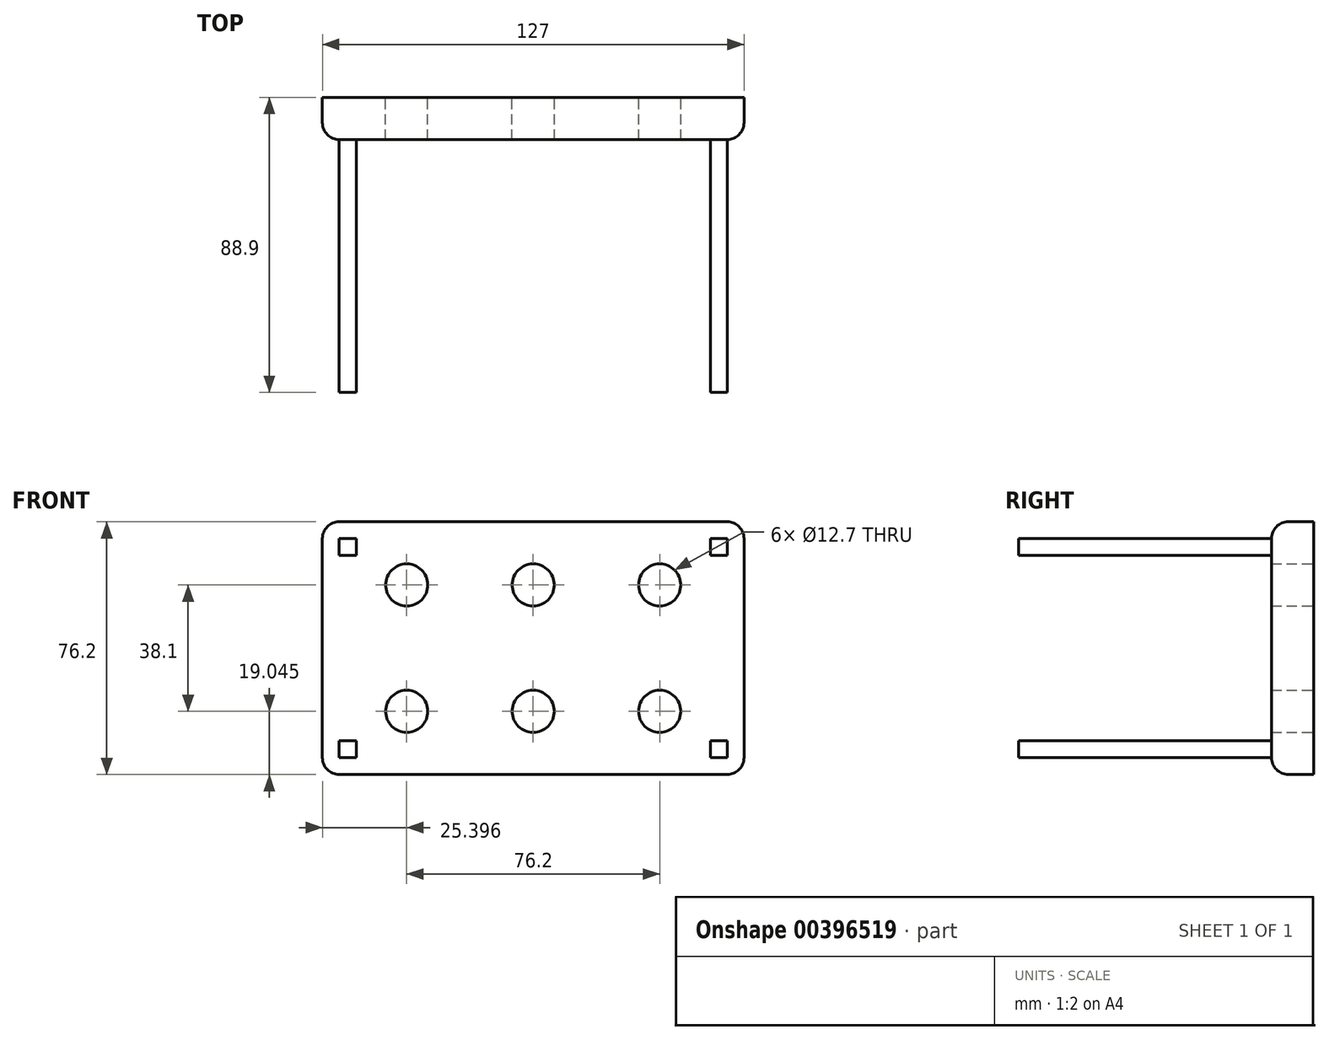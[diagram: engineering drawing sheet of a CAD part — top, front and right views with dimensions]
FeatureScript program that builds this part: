
annotation { "Feature Type Name" : "Feature", "Feature Type Description" : "" }
export const myFeature = defineFeature(function(context is Context, id is Id, definition is map)
    precondition{}
    {
        {
            var Q0;
            Q0=qCreatedBy(makeId("Front.planeOp"),FACE);
            var sketch = newSketch(context, id + "F0", { "sketchPlane" : qUnion([Q0])});
            skLineSegment(sketch, "E0.bottom", {"start": v(-63.95, 33.6) * mm, "end": v(63.05, 33.6) * mm});
            skLineSegment(sketch, "E0.top", {"start": v(-63.95, -42.6) * mm, "end": v(63.05, -42.6) * mm});
            skLineSegment(sketch, "E0.left", {"start": v(-63.95, 33.6) * mm, "end": v(-63.95, -42.6) * mm});
            skLineSegment(sketch, "E0.right", {"start": v(63.05, 33.6) * mm, "end": v(63.05, -42.6) * mm});
            skCircle(sketch, "E1", {"center": v(-38.55, 14.56) * mm, "radius": 6.35 * mm});
            skCircle(sketch, "E2", {"center": v(-0.45, 14.56) * mm, "radius": 6.35 * mm});
            skCircle(sketch, "E3", {"center": v(37.65, 14.56) * mm, "radius": 6.35 * mm});
            skCircle(sketch, "E4", {"center": v(-38.55, -23.54) * mm, "radius": 6.35 * mm});
            skCircle(sketch, "E5", {"center": v(-0.45, -23.54) * mm, "radius": 6.35 * mm});
            skCircle(sketch, "E6", {"center": v(37.65, -23.54) * mm, "radius": 6.35 * mm});
            skSolve(sketch);
        }
        {
            var Q0;
            Q0=makeQuery(id+"F0.imprint","IMPRINT",FACE,{"disambiguationData":[TD([[makeQuery(id+"F0.imprint","IMPRINT",EDGE,{"derivedFrom":sQuery(id+"F0.wireOp",EDGE,"E0.bottom")}),-1.0]])]});
            extrude(context, id + "F1", {"entities" : qUnion([Q0]), "depth" : 12.7 * mm});
        }
        {
            var Q0;
            Q0=makeQuery(id+"F1.opExtrude","CAP_EDGE",EDGE,{"disambiguationData":[OSD([sQuery(id+"F0.wireOp",EDGE,"E0.bottom")])],"isStart":false});
            var Q1;
            Q1=makeQuery(id+"F1.opExtrude","CAP_EDGE",EDGE,{"disambiguationData":[OSD([sQuery(id+"F0.wireOp",EDGE,"E0.left")])],"isStart":false});
            var Q2;
            Q2=makeQuery(id+"F1.opExtrude","CAP_EDGE",EDGE,{"disambiguationData":[OSD([sQuery(id+"F0.wireOp",EDGE,"E0.top")])],"isStart":false});
            var Q3;
            Q3=makeQuery(id+"F1.opExtrude","CAP_EDGE",EDGE,{"disambiguationData":[OSD([sQuery(id+"F0.wireOp",EDGE,"E0.right")])],"isStart":false});
            fillet(context, id + "F2", {"entities" : qUnion([Q0, Q1, Q2, Q3]), "radius" : 5.08 * mm, "tangentPropagation" : true, "allowEdgeOverflow" : false});
        }
        {
            var Q0;
            Q0=makeQuery(id+"F1.opExtrude","SWEPT_EDGE",EDGE,{"disambiguationData":[OSD([sQuery(id+"F0.wireOp",EDGE,"E0.top"),sQuery(id+"F0.wireOp",EDGE,"E0.left")])]});
            var Q1;
            Q1=makeQuery(id+"F1.opExtrude","SWEPT_EDGE",EDGE,{"disambiguationData":[OSD([sQuery(id+"F0.wireOp",EDGE,"E0.top"),sQuery(id+"F0.wireOp",EDGE,"E0.right")])]});
            var Q2;
            Q2=makeQuery(id+"F1.opExtrude","SWEPT_EDGE",EDGE,{"disambiguationData":[OSD([sQuery(id+"F0.wireOp",EDGE,"E0.bottom"),sQuery(id+"F0.wireOp",EDGE,"E0.right")])]});
            var Q3;
            Q3=makeQuery(id+"F1.opExtrude","SWEPT_EDGE",EDGE,{"disambiguationData":[OSD([sQuery(id+"F0.wireOp",EDGE,"E0.bottom"),sQuery(id+"F0.wireOp",EDGE,"E0.left")])]});
            fillet(context, id + "F3", {"entities" : qUnion([Q0, Q1, Q2, Q3]), "radius" : 5.08 * mm, "tangentPropagation" : true, "allowEdgeOverflow" : false});
        }
        {
            var Q0;
            Q0=makeQuery(id+"F1.opExtrude","CAP_FACE",FACE,{"disambiguationData":[OSD([sQuery(id+"F0.wireOp",EDGE,"E0.bottom"),sQuery(id+"F0.wireOp",EDGE,"E0.top"),sQuery(id+"F0.wireOp",EDGE,"E0.left"),sQuery(id+"F0.wireOp",EDGE,"E0.right"),sQuery(id+"F0.wireOp",EDGE,"E1"),sQuery(id+"F0.wireOp",EDGE,"E2"),sQuery(id+"F0.wireOp",EDGE,"E3"),sQuery(id+"F0.wireOp",EDGE,"E4"),sQuery(id+"F0.wireOp",EDGE,"E5"),sQuery(id+"F0.wireOp",EDGE,"E6")])],"isStart":false});
            var sketch = newSketch(context, id + "F4", { "sketchPlane" : qUnion([Q0])});
            skLineSegment(sketch, "E7.bottom", {"start": v(-58.87, 28.53) * mm, "end": v(-53.8, 28.53) * mm});
            skLineSegment(sketch, "E7.top", {"start": v(-58.87, 23.45) * mm, "end": v(-53.8, 23.45) * mm});
            skLineSegment(sketch, "E7.left", {"start": v(-58.87, 28.53) * mm, "end": v(-58.87, 23.45) * mm});
            skLineSegment(sketch, "E7.right", {"start": v(-53.8, 28.53) * mm, "end": v(-53.8, 23.45) * mm});
            skLineSegment(sketch, "E8.bottom", {"start": v(-58.87, -32.43) * mm, "end": v(-53.8, -32.43) * mm});
            skLineSegment(sketch, "E8.top", {"start": v(-58.87, -37.51) * mm, "end": v(-53.8, -37.51) * mm});
            skLineSegment(sketch, "E8.left", {"start": v(-58.87, -32.43) * mm, "end": v(-58.87, -37.51) * mm});
            skLineSegment(sketch, "E8.right", {"start": v(-53.8, -32.43) * mm, "end": v(-53.8, -37.51) * mm});
            skLineSegment(sketch, "E9.bottom", {"start": v(52.89, -32.43) * mm, "end": v(57.97, -32.43) * mm});
            skLineSegment(sketch, "E9.top", {"start": v(52.89, -37.51) * mm, "end": v(57.97, -37.51) * mm});
            skLineSegment(sketch, "E9.left", {"start": v(52.89, -32.43) * mm, "end": v(52.89, -37.51) * mm});
            skLineSegment(sketch, "E9.right", {"start": v(57.97, -32.43) * mm, "end": v(57.97, -37.51) * mm});
            skLineSegment(sketch, "E10.bottom", {"start": v(52.89, 28.53) * mm, "end": v(57.97, 28.53) * mm});
            skLineSegment(sketch, "E10.top", {"start": v(52.89, 23.45) * mm, "end": v(57.97, 23.45) * mm});
            skLineSegment(sketch, "E10.left", {"start": v(52.89, 28.53) * mm, "end": v(52.89, 23.45) * mm});
            skLineSegment(sketch, "E10.right", {"start": v(57.97, 28.53) * mm, "end": v(57.97, 23.45) * mm});
            skSolve(sketch);
        }
        {
            var Q0;
            Q0=makeQuery(id+"F4.imprint","IMPRINT",FACE,{"disambiguationData":[TD([[makeQuery(id+"F4.imprint","IMPRINT",EDGE,{"derivedFrom":sQuery(id+"F4.wireOp",EDGE,"E8.bottom")}),-1.0]])]});
            var Q1;
            Q1=makeQuery(id+"F4.imprint","IMPRINT",FACE,{"disambiguationData":[TD([[makeQuery(id+"F4.imprint","IMPRINT",EDGE,{"derivedFrom":sQuery(id+"F4.wireOp",EDGE,"E9.bottom")}),-1.0]])]});
            var Q2;
            Q2=makeQuery(id+"F4.imprint","IMPRINT",FACE,{"disambiguationData":[TD([[makeQuery(id+"F4.imprint","IMPRINT",EDGE,{"derivedFrom":sQuery(id+"F4.wireOp",EDGE,"E10.bottom")}),1.0]])]});
            var Q3;
            Q3=makeQuery(id+"F4.imprint","IMPRINT",FACE,{"disambiguationData":[TD([[makeQuery(id+"F4.imprint","IMPRINT",EDGE,{"derivedFrom":sQuery(id+"F4.wireOp",EDGE,"E7.bottom")}),1.0]])]});
            extrude(context, id + "F5", {"entities" : qUnion([Q0, Q1, Q2, Q3]), "operationType" : NewBodyOperationType.ADD, "depth" : 76.2 * mm});
        }
    });
